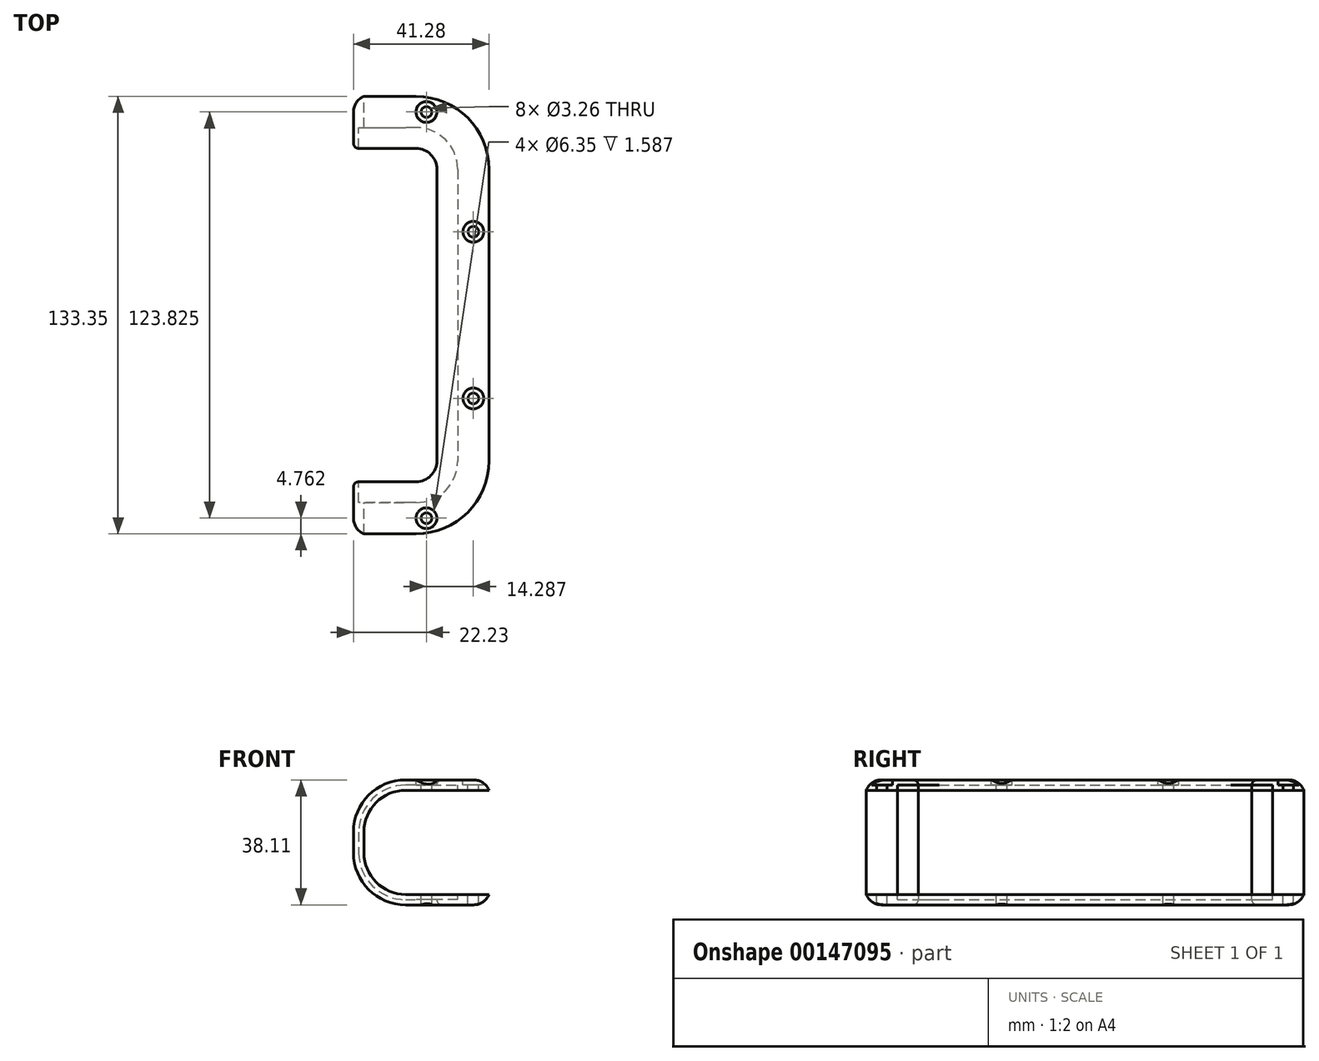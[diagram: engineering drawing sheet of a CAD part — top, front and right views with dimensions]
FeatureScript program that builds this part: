
annotation { "Feature Type Name" : "Feature", "Feature Type Description" : "" }
export const myFeature = defineFeature(function(context is Context, id is Id, definition is map)
    precondition{}
    {
        {
            var Q0;
            Q0=qCreatedBy(makeId("Front.planeOp"),FACE);
            var sketch = newSketch(context, id + "F0", { "sketchPlane" : qUnion([Q0])});
            skLineSegment(sketch, "E0.bottom", {"start": v(0, 0) * mm, "end": v(38.1, 0) * mm});
            skLineSegment(sketch, "E0.top", {"start": v(0, 31.75) * mm, "end": v(38.1, 31.75) * mm});
            skLineSegment(sketch, "E0.left", {"start": v(0, 0) * mm, "end": v(0, 31.75) * mm});
            skLineSegment(sketch, "E0.right", {"start": v(38.1, 0) * mm, "end": v(38.1, 31.75) * mm, "construction": true});
            skLineSegment(sketch, "E1", {"start": v(38.1, 31.75) * mm, "end": v(38.1, 34.93) * mm});
            skLineSegment(sketch, "E2", {"start": v(38.1, 34.93) * mm, "end": v(-3.18, 34.93) * mm});
            skLineSegment(sketch, "E3", {"start": v(-3.18, 34.93) * mm, "end": v(-3.17, -3.17) * mm});
            skLineSegment(sketch, "E4", {"start": v(-3.17, -3.17) * mm, "end": v(38.1, -3.17) * mm});
            skLineSegment(sketch, "E5", {"start": v(38.1, -3.17) * mm, "end": v(38.1, 0) * mm});
            skSolve(sketch);
        }
        {
            var Q0;
            Q0 = qSketchRegion(id + "F0", true);
            extrude(context, id + "F1", {"entities" : qUnion([Q0]), "depth" : 133.35 * mm});
        }
        {
            var Q0;
            Q0=makeQuery(id+"F1.opExtrude","SWEPT_EDGE",EDGE,{"disambiguationData":[OSD([sQuery(id+"F0.wireOp",EDGE,"E0.bottom"),sQuery(id+"F0.wireOp",EDGE,"E0.left")])]});
            var Q1;
            Q1=makeQuery(id+"F1.opExtrude","SWEPT_EDGE",EDGE,{"disambiguationData":[OSD([sQuery(id+"F0.wireOp",EDGE,"E0.top"),sQuery(id+"F0.wireOp",EDGE,"E0.left")])]});
            fillet(context, id + "F2", {"entities" : qUnion([Q0, Q1]), "radius" : 12.7 * mm, "tangentPropagation" : true, "allowEdgeOverflow" : false});
        }
        {
            var Q0;
            Q0=makeQuery(id+"F1.opExtrude","SWEPT_EDGE",EDGE,{"disambiguationData":[OSD([sQuery(id+"F0.wireOp",EDGE,"E3"),sQuery(id+"F0.wireOp",EDGE,"E4")])]});
            var Q1;
            Q1=makeQuery(id+"F1.opExtrude","SWEPT_EDGE",EDGE,{"disambiguationData":[OSD([sQuery(id+"F0.wireOp",EDGE,"E2"),sQuery(id+"F0.wireOp",EDGE,"E3")])]});
            fillet(context, id + "F3", {"entities" : qUnion([Q0, Q1]), "radius" : 15.88 * mm, "tangentPropagation" : true, "allowEdgeOverflow" : false});
        }
        {
            var Q0;
            Q0=makeQuery(id+"F1.opExtrude","CAP_EDGE",EDGE,{"disambiguationData":[OSD([sQuery(id+"F0.wireOp",EDGE,"E1")])],"isStart":false});
            var Q1;
            Q1=makeQuery(id+"F1.opExtrude","CAP_EDGE",EDGE,{"disambiguationData":[OSD([sQuery(id+"F0.wireOp",EDGE,"E5")])],"isStart":false});
            var Q2;
            Q2=makeQuery(id+"F1.opExtrude","CAP_EDGE",EDGE,{"disambiguationData":[OSD([sQuery(id+"F0.wireOp",EDGE,"E1")])],"isStart":true});
            var Q3;
            Q3=makeQuery(id+"F1.opExtrude","CAP_EDGE",EDGE,{"disambiguationData":[OSD([sQuery(id+"F0.wireOp",EDGE,"E5")])],"isStart":true});
            fillet(context, id + "F4", {"entities" : qUnion([Q0, Q1, Q2, Q3]), "radius" : 22.22 * mm, "tangentPropagation" : true, "allowEdgeOverflow" : false});
        }
        {
            var Q0;
            Q0=makeQuery(id+"F1.opExtrude","SWEPT_FACE",FACE,{"disambiguationData":[OSD([sQuery(id+"F0.wireOp",EDGE,"E2")])]});
            var sketch = newSketch(context, id + "F5", { "sketchPlane" : qUnion([Q0])});
            skArc(sketch, "E6", {"start": v(15.87, -117.48) * mm, "mid": v(20.37, -115.62) * mm, "end": v(22.22, -111.13) * mm});
            skArc(sketch, "E7", {"start": v(22.22, -22.22) * mm, "mid": v(20.37, -17.73) * mm, "end": v(15.87, -15.87) * mm});
            skLineSegment(sketch, "E8", {"start": v(-3.17, -117.48) * mm, "end": v(15.87, -117.48) * mm});
            skLineSegment(sketch, "E9", {"start": v(22.22, -111.13) * mm, "end": v(22.22, -22.22) * mm});
            skLineSegment(sketch, "E10", {"start": v(15.87, -15.87) * mm, "end": v(-3.18, -15.87) * mm});
            skLineSegment(sketch, "E11", {"start": v(-3.18, -15.87) * mm, "end": v(-3.17, -117.48) * mm});
            skSolve(sketch);
        }
        {
            var Q0;
            Q0 = qSketchRegion(id + "F5", true);
            extrude(context, id + "F6", {"entities" : qUnion([Q0]), "operationType" : NewBodyOperationType.REMOVE, "endBound" : BoundingType.THROUGH_ALL, "oppositeDirection" : true, "depth" : 25.4 * mm});
        }
        {
            var Q0;
            Q0=makeQuery(id+"F6.boolean.opBoolean","COPY",FACE,{"derivedFrom":makeQuery(id+"F6.opExtrude","SWEPT_FACE",FACE,{"disambiguationData":[OSD([sQuery(id+"F5.wireOp",EDGE,"E8")])]})});
            var sketch = newSketch(context, id + "F7", { "sketchPlane" : qUnion([Q0])});
            skArc(sketch, "E12", {"start": v(-12.7, -1.59) * mm, "mid": v(-2.6, 2.6) * mm, "end": v(1.59, 12.7) * mm});
            skLineSegment(sketch, "E13", {"start": v(1.59, 19.05) * mm, "end": v(1.59, 12.7) * mm});
            skLineSegment(sketch, "E14", {"start": v(-12.7, -1.59) * mm, "end": v(-28.58, -1.59) * mm});
            skLineSegment(sketch, "E15", {"start": v(-28.58, -1.59) * mm, "end": v(-28.58, 33.34) * mm});
            skLineSegment(sketch, "E16", {"start": v(-28.58, 33.34) * mm, "end": v(-12.7, 33.34) * mm});
            skArc(sketch, "E17.trimOffspring", {"start": v(1.59, 19.05) * mm, "mid": v(-2.6, 29.15) * mm, "end": v(-12.7, 33.34) * mm});
            skSolve(sketch);
        }
        {
            var Q0;
            Q0 = qSketchRegion(id + "F7", true);
            extrude(context, id + "F8", {"entities" : qUnion([Q0]), "operationType" : NewBodyOperationType.REMOVE, "oppositeDirection" : true, "depth" : 6.35 * mm, "hasSecondDirection" : true, "secondDirectionOppositeDirection" : false, "secondDirectionDepth" : 107.95 * mm});
        }
        {
            var Q0;
            {var subQ0=sQuery(id+"F7.wireOp",EDGE,"E15");Q0=makeQuery(id+"F8.boolean.opBoolean","COPY",EDGE,{"disambiguationData":[TD([makeQuery(id+"F1.opExtrude","SWEPT_FACE",FACE,{"disambiguationData":[OSD([sQuery(id+"F0.wireOp",EDGE,"E0.bottom")])]})])],"derivedFrom":makeQuery(id+"F8.opExtrude","CAP_EDGE",EDGE,{"disambiguationData":[OSD([subQ0])],"isStart":false})});}
            var Q1;
            {var subQ1=sQuery(id+"F7.wireOp",EDGE,"E15");Q1=makeQuery(id+"F8.boolean.opBoolean","COPY",EDGE,{"disambiguationData":[TD([makeQuery(id+"F1.opExtrude","SWEPT_FACE",FACE,{"disambiguationData":[OSD([sQuery(id+"F0.wireOp",EDGE,"E0.top")])]})])],"derivedFrom":makeQuery(id+"F8.opExtrude","CAP_EDGE",EDGE,{"disambiguationData":[OSD([subQ1])],"isStart":false})});}
            var Q2;
            {var subQ1=sQuery(id+"F7.wireOp",EDGE,"E15");Q2=makeQuery(id+"F8.boolean.opBoolean","COPY",EDGE,{"disambiguationData":[TD([makeQuery(id+"F1.opExtrude","SWEPT_FACE",FACE,{"disambiguationData":[OSD([sQuery(id+"F0.wireOp",EDGE,"E0.top")])]})])],"derivedFrom":makeQuery(id+"F8.opExtrude","CAP_EDGE",EDGE,{"disambiguationData":[OSD([subQ1])],"isStart":true})});}
            var Q3;
            {var subQ0=sQuery(id+"F7.wireOp",EDGE,"E15");Q3=makeQuery(id+"F8.boolean.opBoolean","COPY",EDGE,{"disambiguationData":[TD([makeQuery(id+"F1.opExtrude","SWEPT_FACE",FACE,{"disambiguationData":[OSD([sQuery(id+"F0.wireOp",EDGE,"E0.bottom")])]})])],"derivedFrom":makeQuery(id+"F8.opExtrude","CAP_EDGE",EDGE,{"disambiguationData":[OSD([subQ0])],"isStart":true})});}
            fillet(context, id + "F9", {"entities" : qUnion([Q0, Q1, Q2, Q3]), "radius" : 12.7 * mm, "tangentPropagation" : true, "allowEdgeOverflow" : false});
        }
        {
            var Q0;
            {var subQ0=sQuery(id+"F0.wireOp",EDGE,"E3");var subQ1=sQuery(id+"F0.wireOp",EDGE,"E2");Q0=makeQuery(id+"F3.opFillet","BLEND_EDGE",EDGE,{"blendedFrom":[makeQuery(id+"F1.opExtrude","SWEPT_EDGE",EDGE,{"disambiguationData":[OSD([subQ1,subQ0])]}),makeQuery(id+"F1.opExtrude","CAP_FACE",FACE,{"disambiguationData":[OSD([sQuery(id+"F0.wireOp",EDGE,"E0.bottom"),sQuery(id+"F0.wireOp",EDGE,"E0.top"),sQuery(id+"F0.wireOp",EDGE,"E0.left"),sQuery(id+"F0.wireOp",EDGE,"E1"),subQ1,subQ0,sQuery(id+"F0.wireOp",EDGE,"E4"),sQuery(id+"F0.wireOp",EDGE,"E5")])],"isStart":false})],"blendedInto":[makeQuery(id+"F1.opExtrude","CAP_FACE",FACE,{"disambiguationData":[OSD([sQuery(id+"F0.wireOp",EDGE,"E0.bottom"),sQuery(id+"F0.wireOp",EDGE,"E0.top"),sQuery(id+"F0.wireOp",EDGE,"E0.left"),sQuery(id+"F0.wireOp",EDGE,"E1"),subQ1,subQ0,sQuery(id+"F0.wireOp",EDGE,"E4"),sQuery(id+"F0.wireOp",EDGE,"E5")])],"isStart":false})]});}
            fillet(context, id + "F10", {"entities" : qUnion([Q0]), "radius" : 5.08 * mm, "tangentPropagation" : true, "allowEdgeOverflow" : false});
        }
        {
            var Q0;
            Q0=makeQuery(id+"F6.boolean.opBoolean","INTERSECT",EDGE,{"derivedFrom":[makeQuery(id+"F3.opFillet","BLEND_FACE",FACE,{"disambiguationData":[OSD([sQuery(id+"F0.wireOp",EDGE,"E3"),sQuery(id+"F0.wireOp",EDGE,"E4")])]}),makeQuery(id+"F6.opExtrude","SWEPT_FACE",FACE,{"disambiguationData":[OSD([sQuery(id+"F5.wireOp",EDGE,"E8")])]})]});
            fillet(context, id + "F11", {"entities" : qUnion([Q0]), "radius" : 1.59 * mm, "tangentPropagation" : true, "allowEdgeOverflow" : false});
        }
        {
            var Q0;
            Q0=makeQuery(id+"F1.opExtrude","SWEPT_FACE",FACE,{"disambiguationData":[OSD([sQuery(id+"F0.wireOp",EDGE,"E2")])]});
            var sketch = newSketch(context, id + "F12", { "sketchPlane" : qUnion([Q0])});
            skPoint(sketch, "E18", {"position": v(19.05, -4.76) * mm});
            skPoint(sketch, "E19", {"position": v(33.34, -41.28) * mm});
            skPoint(sketch, "E20", {"position": v(33.34, -92.08) * mm});
            skPoint(sketch, "E21", {"position": v(19.05, -128.59) * mm});
            skLineSegment(sketch, "E22", {"start": v(19.05, -4.76) * mm, "end": v(19.05, -128.59) * mm, "construction": true});
            skLineSegment(sketch, "E23", {"start": v(33.34, -92.08) * mm, "end": v(33.34, -41.28) * mm, "construction": true});
            skLineSegment(sketch, "E24", {"start": v(33.34, -66.68) * mm, "end": v(33.4, -66.68) * mm, "construction": true});
            skLineSegment(sketch, "E25", {"start": v(19.05, -66.68) * mm, "end": v(33.4, -66.68) * mm, "construction": true});
            skSolve(sketch);
        }
        {
            var Q0;
            Q0=sQuery(id+"F12.wireOp",VERTEX,"E18");
            var Q1;
            Q1=sQuery(id+"F12.wireOp",VERTEX,"E19");
            var Q2;
            Q2=sQuery(id+"F12.wireOp",VERTEX,"E20");
            var Q3;
            Q3=sQuery(id+"F12.wireOp",VERTEX,"E21");
            var Q4;
            Q4=makeQuery(id+"F1.opExtrude","SWEPT_BODY",BODY,{"disambiguationData":[OSD([sQuery(id+"F0.wireOp",EDGE,"E0.bottom"),sQuery(id+"F0.wireOp",EDGE,"E0.top"),sQuery(id+"F0.wireOp",EDGE,"E0.left"),sQuery(id+"F0.wireOp",EDGE,"E1"),sQuery(id+"F0.wireOp",EDGE,"E2"),sQuery(id+"F0.wireOp",EDGE,"E3"),sQuery(id+"F0.wireOp",EDGE,"E4"),sQuery(id+"F0.wireOp",EDGE,"E5")])]});
            hole(context, id + "F13", {"style" : HoleStyle.SIMPLE, "endStyle" : HoleEndStyle.THROUGH, "standardTappedOrClearance" : lookupTablePath({ "standard" : "ANSI", "fit" : "Normal (ASME)", "size" : "#4", "type" : "Clearance" }), "standardBlindInLast" : lookupTablePath({ "fit" : "Free", "standard" : "ANSI", "size" : "#4", "type" : "Clearance" }), "holeDiameter" : 3.26 * mm, "locations" : qUnion([Q0, Q1, Q2, Q3]), "scope" : qUnion([Q4]), "isTappedThrough" : true});
        }
        {
            var Q0;
            Q0=makeQuery(id+"F1.opExtrude","SWEPT_FACE",FACE,{"disambiguationData":[OSD([sQuery(id+"F0.wireOp",EDGE,"E2")])]});
            var sketch = newSketch(context, id + "F14", { "sketchPlane" : qUnion([Q0])});
            skCircle(sketch, "E26", {"center": v(19.05, -4.76) * mm, "radius": 3.18 * mm});
            skCircle(sketch, "E27", {"center": v(33.34, -41.28) * mm, "radius": 3.18 * mm});
            skCircle(sketch, "E28", {"center": v(33.34, -92.08) * mm, "radius": 3.18 * mm});
            skCircle(sketch, "E29", {"center": v(19.05, -128.59) * mm, "radius": 3.18 * mm});
            skSolve(sketch);
        }
        {
            var Q0;
            Q0 = qSketchRegion(id + "F14", true);
            extrude(context, id + "F15", {"entities" : qUnion([Q0]), "operationType" : NewBodyOperationType.REMOVE, "oppositeDirection" : true, "depth" : 1.59 * mm});
        }
    });
